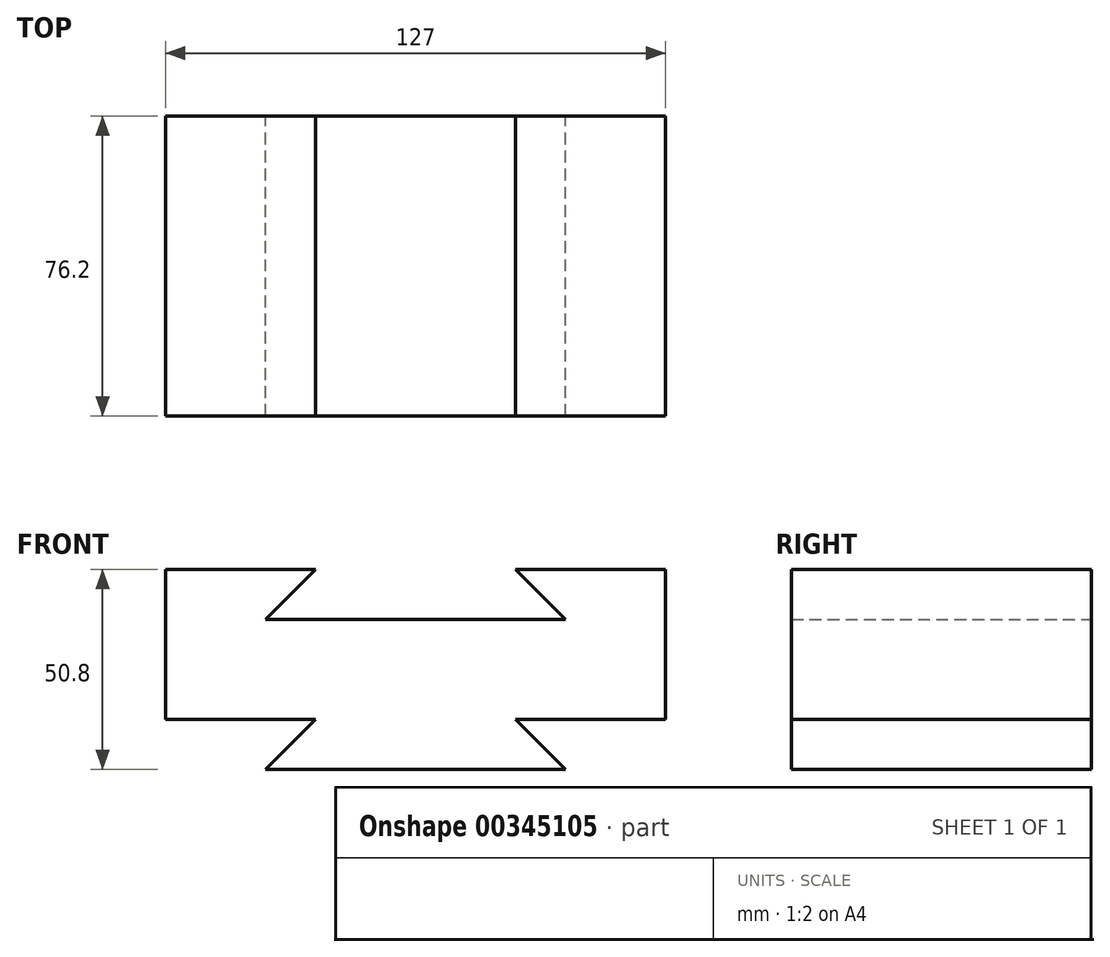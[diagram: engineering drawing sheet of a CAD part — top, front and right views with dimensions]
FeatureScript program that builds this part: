
annotation { "Feature Type Name" : "Feature", "Feature Type Description" : "" }
export const myFeature = defineFeature(function(context is Context, id is Id, definition is map)
    precondition{}
    {
        {
            var Q0;
            Q0=qCreatedBy(makeId("Front.planeOp"),FACE);
            var sketch = newSketch(context, id + "F0", { "sketchPlane" : qUnion([Q0])});
            skLineSegment(sketch, "E0", {"start": v(0, 0) * mm, "end": v(0, 38.1) * mm});
            skLineSegment(sketch, "E1", {"start": v(0, 38.1) * mm, "end": v(38.1, 38.1) * mm});
            skLineSegment(sketch, "E2", {"start": v(38.1, 38.1) * mm, "end": v(25.4, 25.4) * mm});
            skLineSegment(sketch, "E3", {"start": v(25.4, 25.4) * mm, "end": v(101.6, 25.4) * mm});
            skLineSegment(sketch, "E4", {"start": v(101.6, 25.4) * mm, "end": v(88.9, 38.1) * mm});
            skLineSegment(sketch, "E5", {"start": v(88.9, 38.1) * mm, "end": v(127, 38.1) * mm});
            skLineSegment(sketch, "E6", {"start": v(127, 38.1) * mm, "end": v(127, 0) * mm});
            skLineSegment(sketch, "E7", {"start": v(127, 0) * mm, "end": v(88.9, 0) * mm});
            skLineSegment(sketch, "E8", {"start": v(88.9, 0) * mm, "end": v(101.6, -12.7) * mm});
            skLineSegment(sketch, "E9", {"start": v(101.6, -12.7) * mm, "end": v(25.4, -12.7) * mm});
            skLineSegment(sketch, "E10", {"start": v(25.4, -12.7) * mm, "end": v(38.1, 0) * mm});
            skLineSegment(sketch, "E11", {"start": v(38.1, 0) * mm, "end": v(0, 0) * mm});
            skSolve(sketch);
        }
        {
            var Q0;
            Q0 = qSketchRegion(id + "F0", true);
            extrude(context, id + "F1", {"entities" : qUnion([Q0]), "depth" : 76.2 * mm});
        }
    });
